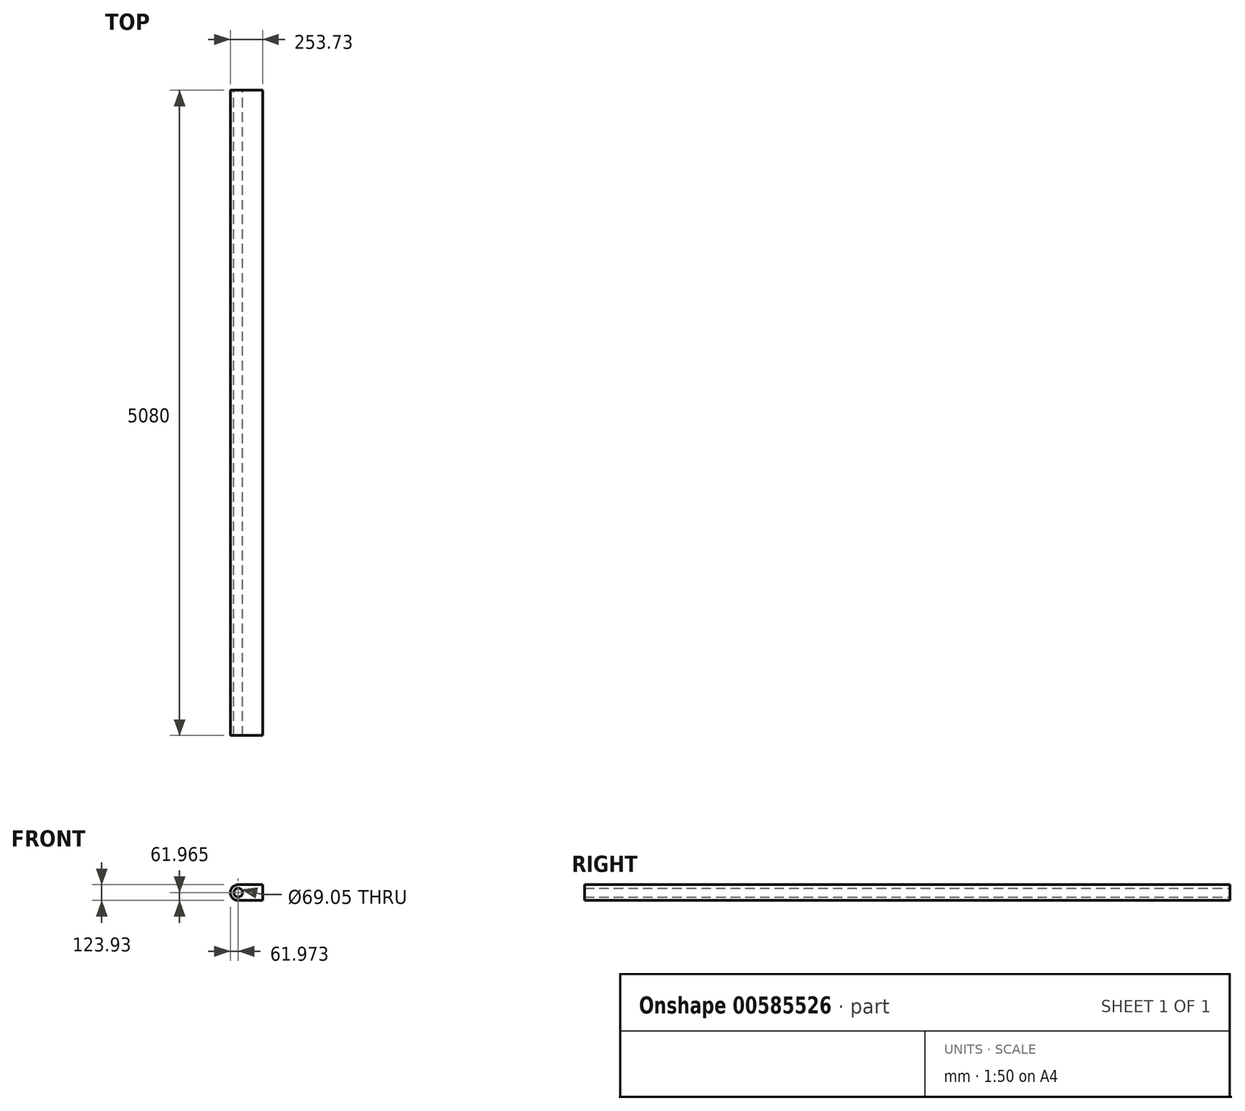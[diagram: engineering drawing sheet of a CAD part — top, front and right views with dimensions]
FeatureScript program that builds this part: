
annotation { "Feature Type Name" : "Feature", "Feature Type Description" : "" }
export const myFeature = defineFeature(function(context is Context, id is Id, definition is map)
    precondition{}
    {
        {
            var Q0;
            Q0=qCreatedBy(makeId("Front.planeOp"),FACE);
            var sketch = newSketch(context, id + "F0", { "sketchPlane" : qUnion([Q0])});
            skLineSegment(sketch, "E0.bottom", {"start": v(-95.88, -66.35) * mm, "end": v(95.88, -66.35) * mm});
            skLineSegment(sketch, "E0.top", {"start": v(-95.88, 57.58) * mm, "end": v(95.88, 57.58) * mm});
            skLineSegment(sketch, "E0.left", {"start": v(-95.88, -66.35) * mm, "end": v(-95.88, 57.58) * mm});
            skLineSegment(sketch, "E0.right", {"start": v(95.88, -66.35) * mm, "end": v(95.88, 57.58) * mm});
            skPoint(sketch, "E0.middle", {"position": v(0, -4.38) * mm});
            skCircle(sketch, "E1", {"center": v(-95.88, -4.38) * mm, "radius": 61.97 * mm});
            skCircle(sketch, "E2", {"center": v(-95.88, -4.38) * mm, "radius": 34.53 * mm});
            skSolve(sketch);
        }
        {
            var Q0;
            Q0 = qSketchRegion(id + "F0", true);
            extrude(context, id + "F1", {"entities" : qUnion([Q0]), "endBound" : BoundingType.SYMMETRIC, "depth" : 5080 * mm, "offsetDistance" : 25.4 * mm});
        }
    });
